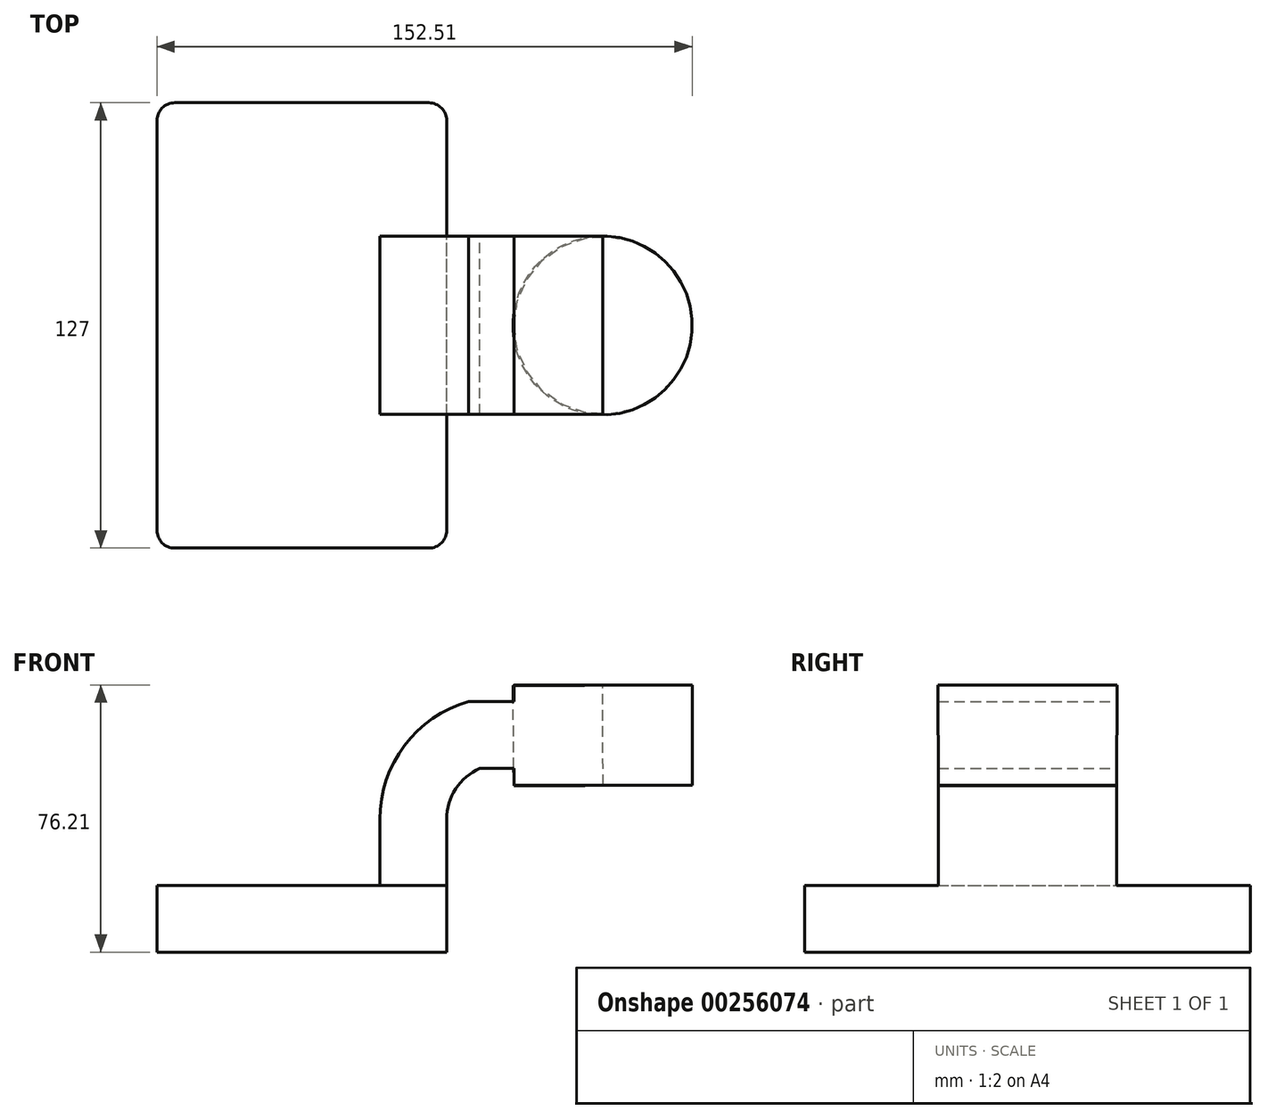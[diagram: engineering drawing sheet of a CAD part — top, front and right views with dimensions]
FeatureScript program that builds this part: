
annotation { "Feature Type Name" : "Feature", "Feature Type Description" : "" }
export const myFeature = defineFeature(function(context is Context, id is Id, definition is map)
    precondition{}
    {
        {
            var Q0;
            Q0=qCreatedBy(makeId("Front.planeOp"),FACE);
            var sketch = newSketch(context, id + "F0", { "sketchPlane" : qUnion([Q0])});
            skLineSegment(sketch, "E0.bottom", {"start": v(41.27, 9.53) * mm, "end": v(-41.28, 9.53) * mm});
            skLineSegment(sketch, "E0.top", {"start": v(41.28, -9.52) * mm, "end": v(-41.28, -9.52) * mm});
            skLineSegment(sketch, "E0.left", {"start": v(41.28, 9.53) * mm, "end": v(41.28, -9.52) * mm});
            skLineSegment(sketch, "E0.right", {"start": v(-41.28, 9.53) * mm, "end": v(-41.28, -9.52) * mm});
            skPoint(sketch, "E0.middle", {"position": v(0, 0) * mm});
            skLineSegment(sketch, "E1.bottom", {"start": v(111.24, 66.68) * mm, "end": v(60.44, 66.68) * mm});
            skLineSegment(sketch, "E1.top", {"start": v(111.24, 38.1) * mm, "end": v(60.44, 38.1) * mm});
            skLineSegment(sketch, "E1.left", {"start": v(111.24, 66.67) * mm, "end": v(111.24, 38.1) * mm});
            skLineSegment(sketch, "E1.right", {"start": v(60.44, 66.67) * mm, "end": v(60.44, 38.1) * mm});
            skPoint(sketch, "E1.middle", {"position": v(85.84, 52.39) * mm});
            skLineSegment(sketch, "E2", {"start": v(41.27, 9.53) * mm, "end": v(41.27, 28.34) * mm});
            skArc(sketch, "E3", {"start": v(41.27, 28.34) * mm, "mid": v(43.86, 37.02) * mm, "end": v(50.76, 42.88) * mm});
            skLineSegment(sketch, "E4", {"start": v(50.76, 42.88) * mm, "end": v(85.72, 42.88) * mm});
            skLineSegment(sketch, "E5.0", {"start": v(47.56, 61.93) * mm, "end": v(85.72, 61.93) * mm});
            skArc(sketch, "E5.1", {"start": v(22.22, 28.34) * mm, "mid": v(29.27, 49.38) * mm, "end": v(47.56, 61.93) * mm});
            skLineSegment(sketch, "E5.2", {"start": v(22.22, 9.53) * mm, "end": v(22.22, 28.34) * mm});
            skLineSegment(sketch, "E6", {"start": v(85.84, 38.1) * mm, "end": v(85.72, 66.68) * mm});
            skFitSpline(sketch, "E7", {"points": [v(-41.28, 9.53) * mm, v(47.56, 61.93) * mm], "startDerivative": vector(4.2, 56.35) * mm, "endDerivative": vector(153.34, 5.52) * mm});
            skSolve(sketch);
        }
        {
            var Q0;
            Q0=makeQuery(id+"F0.imprint","IMPRINT",FACE,{"disambiguationData":[TD([[makeQuery(id+"F0.imprint","IMPRINT",EDGE,{"derivedFrom":sQuery(id+"F0.wireOp",EDGE,"E0.top")}),-1.0]])]});
            extrude(context, id + "F1", {"entities" : qUnion([Q0]), "endBound" : BoundingType.SYMMETRIC, "depth" : 127 * mm});
        }
        {
            var Q0;
            {var subQ2=sQuery(id+"F0.wireOp",EDGE,"E2");Q0=makeQuery(id+"F0.imprint","IMPRINT",FACE,{"disambiguationData":[TD([[makeQuery(id+"F0.imprint","IMPRINT",EDGE,{"derivedFrom":subQ2}),1.0]])]});}
            var Q1;
            {var subQ7=sQuery(id+"F0.wireOp",EDGE,"E6");Q1=makeQuery(id+"F0.imprint","IMPRINT",FACE,{"disambiguationData":[TD([[makeQuery(id+"F0.imprint","IMPRINT",EDGE,{"derivedFrom":subQ7}),1.0]])]});}
            extrude(context, id + "F2", {"entities" : qUnion([Q0, Q1]), "operationType" : NewBodyOperationType.ADD, "endBound" : BoundingType.SYMMETRIC, "depth" : 50.8 * mm});
        }
        {
            var Q0;
            Q0=makeQuery(id+"F0.imprint","IMPRINT",FACE,{"disambiguationData":[TD([[makeQuery(id+"F0.imprint","IMPRINT",EDGE,{"derivedFrom":sQuery(id+"F0.wireOp",EDGE,"E5.1")}),1.0]])]});
            extrude(context, id + "F3", {"entities" : qUnion([Q0]), "operationType" : NewBodyOperationType.ADD, "endBound" : BoundingType.SYMMETRIC, "depth" : 15.88 * mm});
        }
        {
            var Q0;
            {var subQ0=sQuery(id+"F0.wireOp",EDGE,"E1.left");Q0=makeQuery(id+"F0.imprint","IMPRINT",FACE,{"disambiguationData":[TD([[makeQuery(id+"F0.imprint","IMPRINT",EDGE,{"derivedFrom":subQ0}),-1.0]])]});}
            var Q1;
            Q1=sQuery(id+"F0.wireOp",EDGE,"E6");
            revolve(context, id + "F4", {"entities" : qUnion([Q0]), "axis" : qUnion([Q1]), "revolveType" : RevolveType.FULL});
        }
        {
            var Q0;
            Q0=makeQuery(id+"F1.opExtrude","CAP_EDGE",EDGE,{"disambiguationData":[OSD([sQuery(id+"F0.wireOp",EDGE,"E0.right")])],"isStart":false});
            var Q1;
            Q1=makeQuery(id+"F1.opExtrude","CAP_EDGE",EDGE,{"disambiguationData":[OSD([sQuery(id+"F0.wireOp",EDGE,"E0.left")])],"isStart":false});
            var Q2;
            Q2=makeQuery(id+"F1.opExtrude","CAP_EDGE",EDGE,{"disambiguationData":[OSD([sQuery(id+"F0.wireOp",EDGE,"E0.left")])],"isStart":true});
            var Q3;
            Q3=makeQuery(id+"F1.opExtrude","CAP_EDGE",EDGE,{"disambiguationData":[OSD([sQuery(id+"F0.wireOp",EDGE,"E0.right")])],"isStart":true});
            fillet(context, id + "F5", {"entities" : qUnion([Q0, Q1, Q2, Q3]), "radius" : 5.08 * mm, "tangentPropagation" : true, "allowEdgeOverflow" : false});
        }
    });
